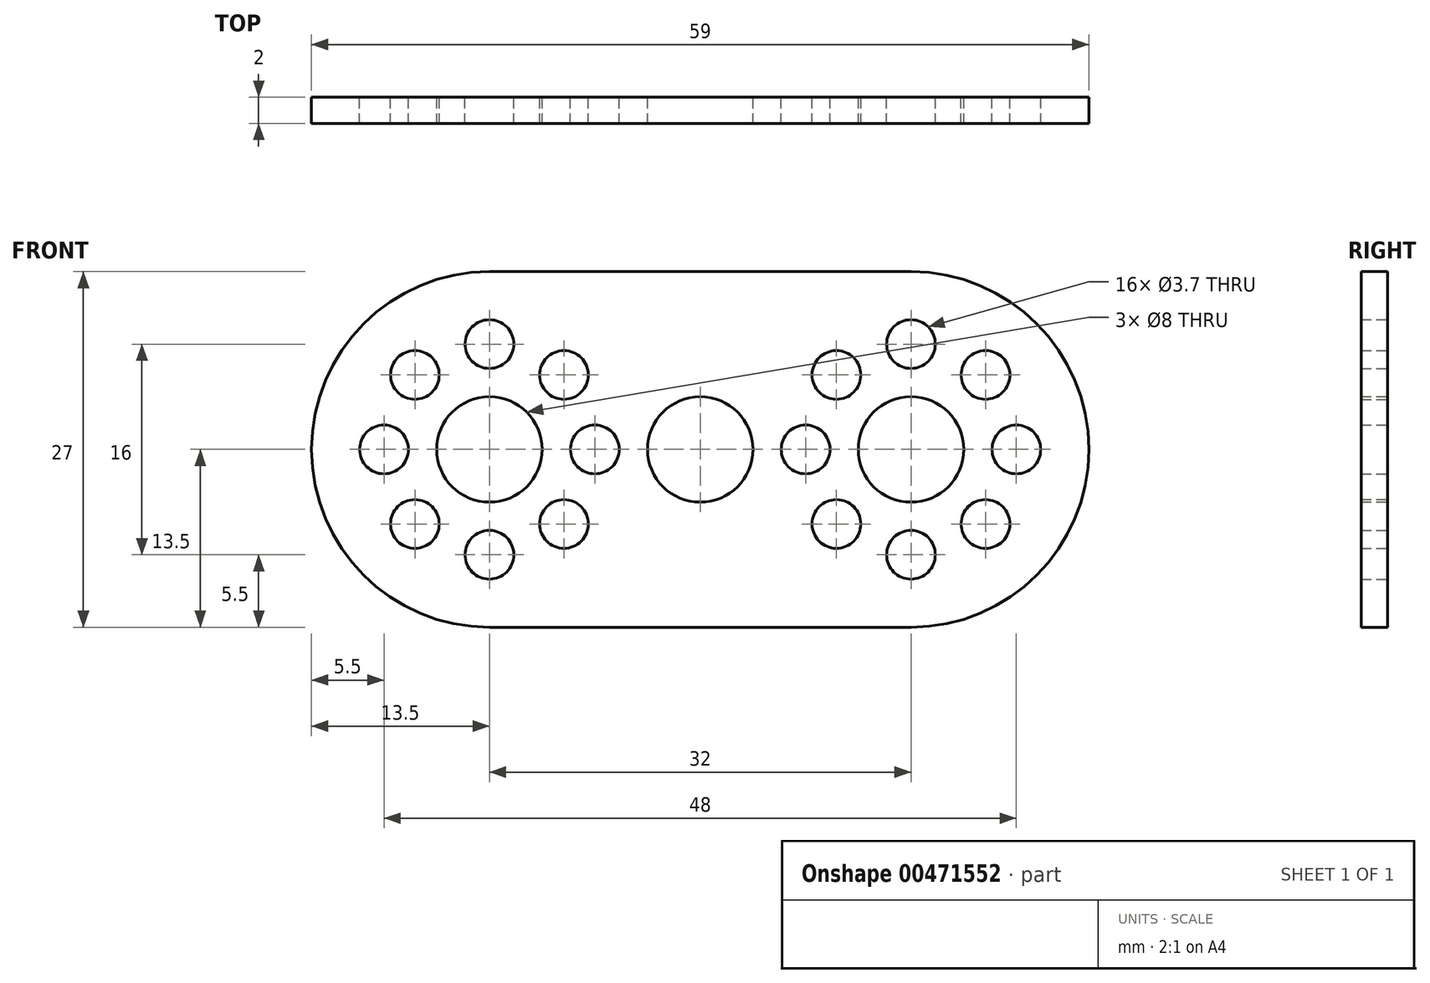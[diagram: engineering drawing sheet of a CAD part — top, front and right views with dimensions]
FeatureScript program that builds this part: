
annotation { "Feature Type Name" : "Feature", "Feature Type Description" : "" }
export const myFeature = defineFeature(function(context is Context, id is Id, definition is map)
    precondition{}
    {
        {
            var Q0;
            Q0=qCreatedBy(makeId("Front.planeOp"),FACE);
            var sketch = newSketch(context, id + "F0", { "sketchPlane" : qUnion([Q0])});
            skLineSegment(sketch, "E0.bottom", {"start": v(16, 13.5) * mm, "end": v(-16, 13.5) * mm});
            skLineSegment(sketch, "E0.top", {"start": v(16, -13.5) * mm, "end": v(-16, -13.5) * mm});
            skLineSegment(sketch, "E0.left", {"start": v(29.5, 0) * mm, "end": v(29.5, 0) * mm});
            skLineSegment(sketch, "E0.right", {"start": v(-29.5, 0) * mm, "end": v(-29.5, 0) * mm});
            skPoint(sketch, "E0.middle", {"position": v(0, 0) * mm});
            skCircle(sketch, "E1", {"center": v(0, 0) * mm, "radius": 4 * mm});
            skCircle(sketch, "E2", {"center": v(16, 0) * mm, "radius": 4 * mm});
            skCircle(sketch, "E3", {"center": v(16, 8) * mm, "radius": 1.85 * mm});
            skCircle(sketch, "E4.1.0", {"center": v(10.34, 5.66) * mm, "radius": 1.85 * mm});
            skCircle(sketch, "E4.2.0", {"center": v(8, 0) * mm, "radius": 1.85 * mm});
            skCircle(sketch, "E4.3.0", {"center": v(10.34, -5.66) * mm, "radius": 1.85 * mm});
            skCircle(sketch, "E4.4.0", {"center": v(16, -8) * mm, "radius": 1.85 * mm});
            skCircle(sketch, "E4.5.0", {"center": v(21.66, -5.66) * mm, "radius": 1.85 * mm});
            skCircle(sketch, "E4.6.0", {"center": v(24, 0) * mm, "radius": 1.85 * mm});
            skCircle(sketch, "E4.7.0", {"center": v(21.66, 5.66) * mm, "radius": 1.85 * mm});
            skCircle(sketch, "E5.MirrorC", {"center": v(-16, 0) * mm, "radius": 4 * mm});
            skCircle(sketch, "E6.MirrorC", {"center": v(-21.66, 5.66) * mm, "radius": 1.85 * mm});
            skCircle(sketch, "E7.MirrorC", {"center": v(-10.34, -5.66) * mm, "radius": 1.85 * mm});
            skCircle(sketch, "E8.MirrorC", {"center": v(-21.66, -5.66) * mm, "radius": 1.85 * mm});
            skCircle(sketch, "E9.MirrorC", {"center": v(-10.34, 5.66) * mm, "radius": 1.85 * mm});
            skCircle(sketch, "E10.MirrorC", {"center": v(-16, 8) * mm, "radius": 1.85 * mm});
            skCircle(sketch, "E11.MirrorC", {"center": v(-24, 0) * mm, "radius": 1.85 * mm});
            skCircle(sketch, "E12.MirrorC", {"center": v(-16, -8) * mm, "radius": 1.85 * mm});
            skCircle(sketch, "E13.MirrorC", {"center": v(-8, 0) * mm, "radius": 1.85 * mm});
            skPoint(sketch, "E14.visualSharp", {"position": v(29.5, 13.5) * mm});
            skArc(sketch, "E14.filletArc", {"start": v(29.5, 0) * mm, "mid": v(25.55, 9.55) * mm, "end": v(16, 13.5) * mm});
            skPoint(sketch, "E15.visualSharp", {"position": v(29.5, -13.5) * mm});
            skArc(sketch, "E15.filletArc", {"start": v(16, -13.5) * mm, "mid": v(25.55, -9.55) * mm, "end": v(29.5, 0) * mm});
            skPoint(sketch, "E16.visualSharp", {"position": v(-29.5, 13.5) * mm});
            skArc(sketch, "E16.filletArc", {"start": v(-16, 13.5) * mm, "mid": v(-25.55, 9.55) * mm, "end": v(-29.5, 0) * mm});
            skPoint(sketch, "E17.visualSharp", {"position": v(-29.5, -13.5) * mm});
            skArc(sketch, "E17.filletArc", {"start": v(-29.5, 0) * mm, "mid": v(-25.55, -9.55) * mm, "end": v(-16, -13.5) * mm});
            skSolve(sketch);
        }
        {
            var Q0;
            Q0=makeQuery(id+"F0.imprint","IMPRINT",FACE,{"disambiguationData":[TD([[makeQuery(id+"F0.imprint","IMPRINT",EDGE,{"derivedFrom":sQuery(id+"F0.wireOp",EDGE,"E0.bottom")}),1.0]])]});
            extrude(context, id + "F1", {"entities" : qUnion([Q0]), "depth" : 2 * mm});
        }
    });
